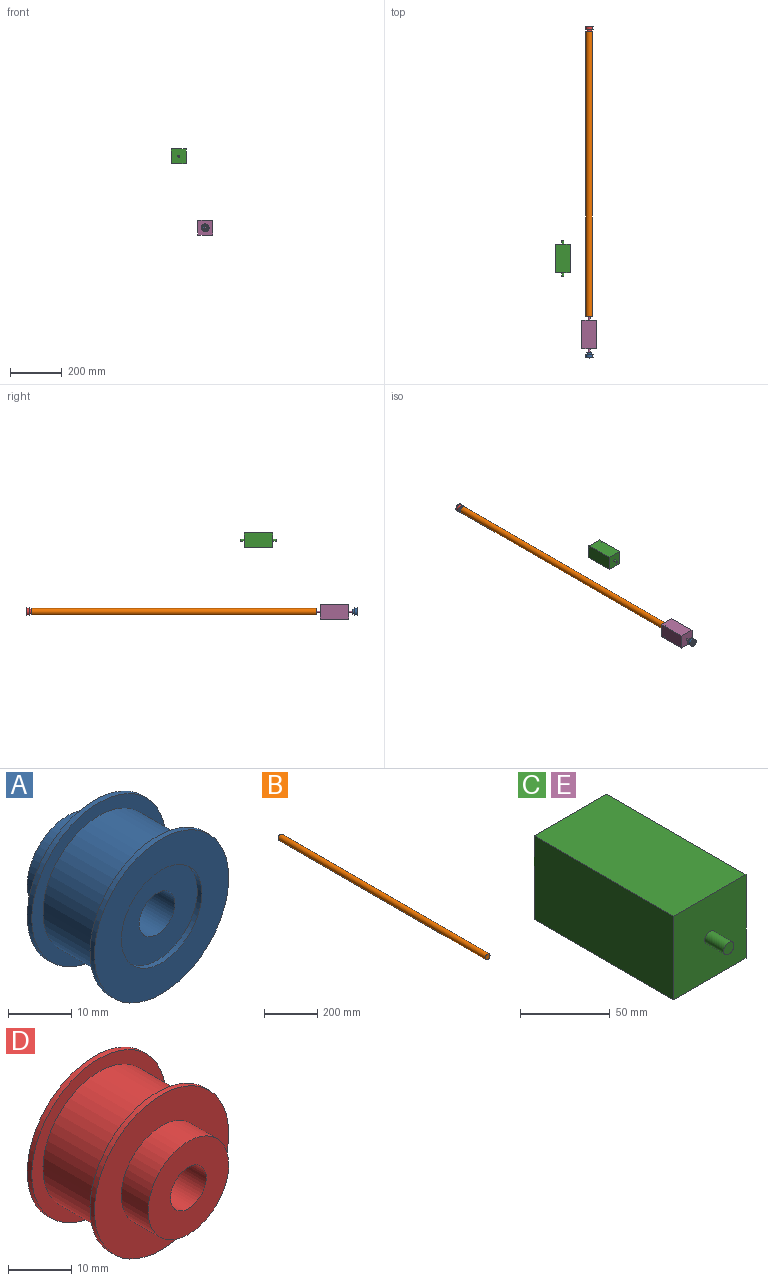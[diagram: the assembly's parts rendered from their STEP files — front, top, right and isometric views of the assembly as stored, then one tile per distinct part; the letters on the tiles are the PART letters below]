
ASSEMBLY  parts=5 mates=4
PART A: 12 faces, bbox 30x21x30 mm
  f0: cylinder r=9mm len=18mm, axis (0,1,0), area 56.5mm2, adj f6,f10
  f1: cylinder r=12.5mm len=25mm, axis (0,1,0), area 1021mm2, adj f4,f7
  f2: plane 30x30mm, normal (0,1,0), area 452.4mm2, adj f3,f9
  f3: cylinder r=15mm len=30mm, axis (0,1,0), area 94.2mm2, adj f2,f4
  f4: plane 30x30mm, normal (0,-1,0), area 216mm2, adj f1,f3
  f5: cylinder r=15mm len=30mm, axis (0,1,0), area 94.2mm2, adj f6,f7
  f6: plane 30x30mm, normal (0,-1,0), area 452.4mm2, adj f0,f5
  f7: plane 30x30mm, normal (0,1,0), area 216mm2, adj f1,f5
  f8: plane 18x18mm, normal (0,1,0), area 204.2mm2, adj f9,f11
  f9: cylinder r=9mm len=18mm, axis (0,-1,0), area 339.3mm2, adj f2,f8
  f10: plane 18x18mm, normal (0,-1,0), area 204.2mm2, adj f0,f11
  f11: cylinder r=4mm len=20mm, axis (0,-1,0), area 502.7mm2, adj f8,f10
PART B: 3 faces, bbox 25x1100x25 mm
  f0: cylinder r=12.5mm len=1100mm, axis (0,1,0), area 86393.8mm2, adj f1,f2
  f1: plane 25x25mm, normal (0,-1,0), area 490.9mm2, adj f0
  f2: plane 25x25mm, normal (0,1,0), area 490.9mm2, adj f0
PART C: 18 faces, bbox 57x140x57 mm
  f0: cylinder r=4mm len=15mm, axis (0,1,0), area 377mm2, adj f1,f6
  f1: plane 8x8mm, normal (0,-1,0), area 50.3mm2, adj f0
  f2: plane 110x57mm, normal (1,0,0), area 6270mm2, adj f3,f5,f6,f7
  f3: plane 110x57mm, normal (0,0,1), area 6270mm2, adj f2,f4,f6,f7
  f4: plane 110x57mm, normal (-1,0,0), area 6270mm2, adj f3,f5,f6,f7
  f5: plane 110x57mm, normal (0,0,-1), area 6270mm2, adj f2,f4,f6,f7
  f6: plane 57x57mm, normal (0,-1,0), area 3198.7mm2, adj f0,f2,f3,f4,f5
  f7: plane 57x57mm, normal (0,1,0), area 3085.6mm2, adj f2,f3,f4,f5,f9,f11,f13,f15
  f8: plane 8x8mm, normal (0,1,0), area 50.3mm2, adj f9
  f9: cylinder r=4mm len=15mm, axis (0,1,0), area 377mm2, adj f7,f8
  f10: cone r=0mm half-angle=59deg, axis (0,1,0), area 33mm2, adj f11
  f11: cylinder r=3mm len=16mm, axis (0,1,0), area 301.6mm2, adj f7,f10
  f12: cone r=0mm half-angle=59deg, axis (0,1,0), area 33mm2, adj f13
  f13: cylinder r=3mm len=16mm, axis (0,1,0), area 301.6mm2, adj f7,f12
  f14: cone r=0mm half-angle=59deg, axis (0,1,0), area 33mm2, adj f15
  f15: cylinder r=3mm len=16mm, axis (0,1,0), area 301.6mm2, adj f7,f14
  f16: cone r=0mm half-angle=59deg, axis (0,1,0), area 33mm2, adj f17
  f17: cylinder r=3mm len=16mm, axis (0,1,0), area 301.6mm2, adj f7,f16
PART D: 12 faces, bbox 30x21x30 mm
  f0: cylinder r=9mm len=18mm, axis (0,-1,0), area 56.5mm2, adj f6,f10
  f1: cylinder r=12.5mm len=25mm, axis (0,-1,0), area 1021mm2, adj f4,f7
  f2: plane 30x30mm, normal (0,-1,0), area 452.4mm2, adj f3,f9
  f3: cylinder r=15mm len=30mm, axis (0,-1,0), area 94.2mm2, adj f2,f4
  f4: plane 30x30mm, normal (0,1,0), area 216mm2, adj f1,f3
  f5: cylinder r=15mm len=30mm, axis (0,-1,0), area 94.2mm2, adj f6,f7
  f6: plane 30x30mm, normal (0,1,0), area 452.4mm2, adj f0,f5
  f7: plane 30x30mm, normal (0,-1,0), area 216mm2, adj f1,f5
  f8: plane 18x18mm, normal (0,-1,0), area 204.2mm2, adj f9,f11
  f9: cylinder r=9mm len=18mm, axis (0,1,0), area 339.3mm2, adj f2,f8
  f10: plane 18x18mm, normal (0,1,0), area 204.2mm2, adj f0,f11
  f11: cylinder r=4mm len=20mm, axis (0,1,0), area 502.7mm2, adj f8,f10
PART E: same geometry as C
PLACE A t=(27.04,-219.89,13.56)mm
PLACE B t=(27.04,1026.11,13.56)mm
PLACE C t=(-74.88,204.71,289.42)mm
PLACE D t=(27.04,1062.11,13.56)mm
PLACE E t=(27.04,-88.89,13.56)mm fixed
MATE fastened E.f0 <-> A.f11  axis (0,-1,0) through (27.04,-213.89,13.56)mm
MATE fastened E.f0 <-> D.f11  axis (0,1,0) through (27.04,-73.89,13.56)mm
MATE slider E.f0 <-> B.f0  axis (0,1,0) through (27.04,-73.89,13.56)mm
MATE fastened D.f11 <-> B.f0  axis (0,1,0) through (27.04,1026.11,13.56)mm
